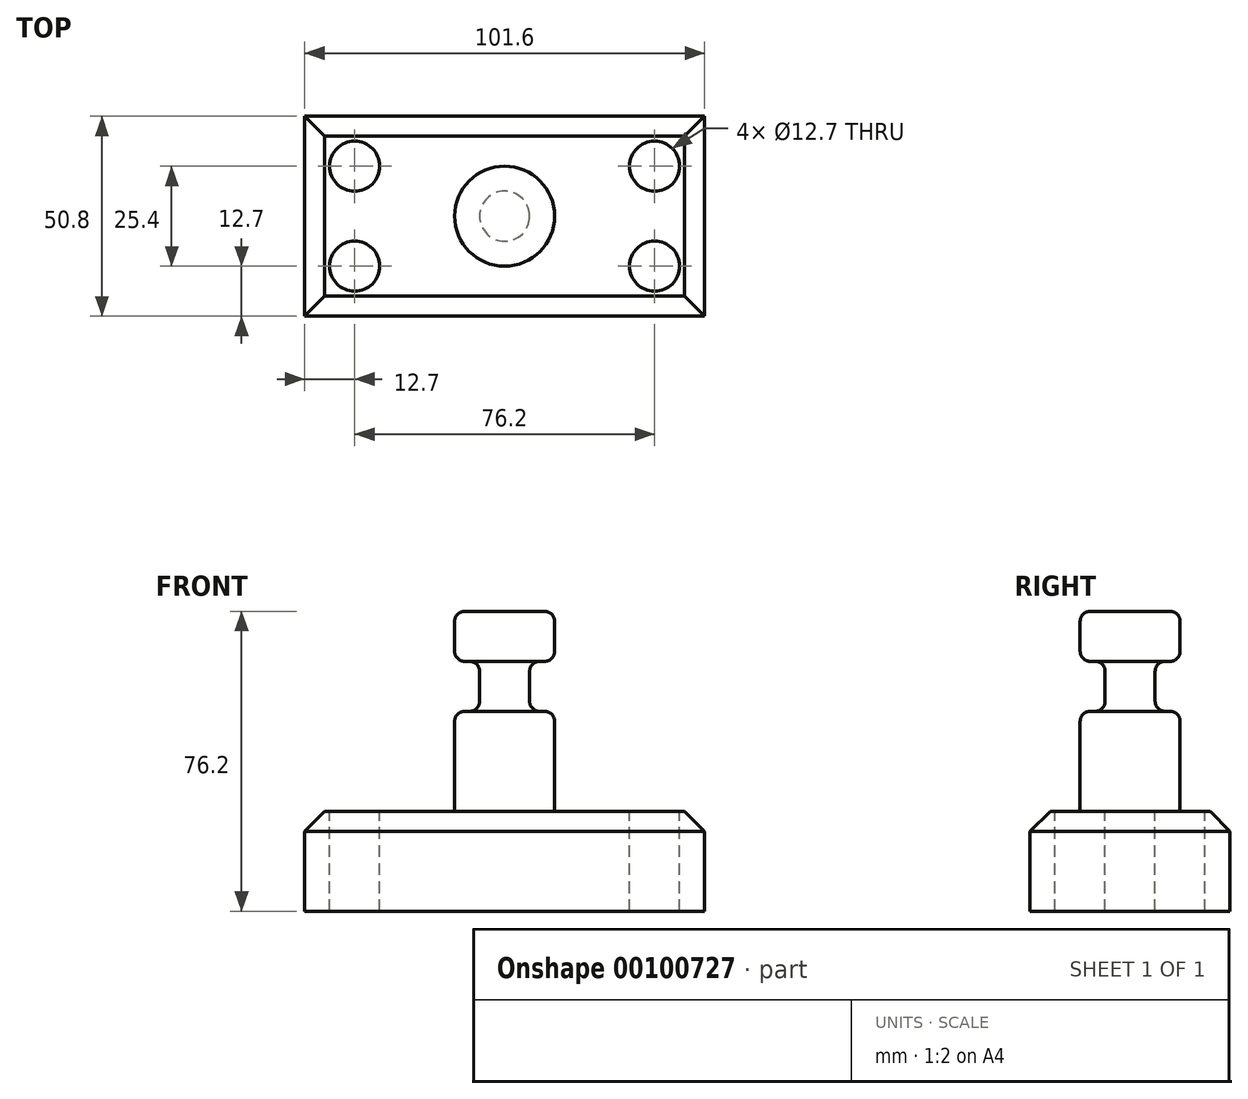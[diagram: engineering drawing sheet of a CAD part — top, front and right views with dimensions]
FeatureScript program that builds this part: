
annotation { "Feature Type Name" : "Feature", "Feature Type Description" : "" }
export const myFeature = defineFeature(function(context is Context, id is Id, definition is map)
    precondition{}
    {
        {
            var Q0;
            Q0=qCreatedBy(makeId("Top.planeOp"),FACE);
            var sketch = newSketch(context, id + "F0", { "sketchPlane" : qUnion([Q0])});
            skLineSegment(sketch, "E0.bottom", {"start": v(-50.8, 25.4) * mm, "end": v(50.8, 25.4) * mm});
            skLineSegment(sketch, "E0.top", {"start": v(-50.8, -25.4) * mm, "end": v(50.8, -25.4) * mm});
            skLineSegment(sketch, "E0.left", {"start": v(-50.8, 25.4) * mm, "end": v(-50.8, -25.4) * mm});
            skLineSegment(sketch, "E0.right", {"start": v(50.8, 25.4) * mm, "end": v(50.8, -25.4) * mm});
            skPoint(sketch, "E0.middle", {"position": v(0, 0) * mm});
            skSolve(sketch);
        }
        {
            var Q0;
            Q0=makeQuery(id+"F0.imprint","IMPRINT",FACE,{"disambiguationData":[TD([[makeQuery(id+"F0.imprint","IMPRINT",EDGE,{"derivedFrom":sQuery(id+"F0.wireOp",EDGE,"E0.bottom")}),-1.0]])]});
            extrude(context, id + "F1", {"entities" : qUnion([Q0]), "depth" : 25.4 * mm});
        }
        {
            var Q0;
            Q0=makeQuery(id+"F1.opExtrude","CAP_FACE",FACE,{"disambiguationData":[OSD([sQuery(id+"F0.wireOp",EDGE,"E0.bottom"),sQuery(id+"F0.wireOp",EDGE,"E0.top"),sQuery(id+"F0.wireOp",EDGE,"E0.left"),sQuery(id+"F0.wireOp",EDGE,"E0.right")])],"isStart":false});
            var sketch = newSketch(context, id + "F2", { "sketchPlane" : qUnion([Q0])});
            skCircle(sketch, "E1", {"center": v(-38.1, 12.7) * mm, "radius": 6.35 * mm});
            skCircle(sketch, "E2", {"center": v(38.1, 12.7) * mm, "radius": 6.35 * mm});
            skCircle(sketch, "E3", {"center": v(38.1, -12.7) * mm, "radius": 6.35 * mm});
            skCircle(sketch, "E4", {"center": v(-38.1, -12.7) * mm, "radius": 6.35 * mm});
            skSolve(sketch);
        }
        {
            var Q0;
            Q0 = qSketchRegion(id + "F2", true);
            extrude(context, id + "F3", {"entities" : qUnion([Q0]), "operationType" : NewBodyOperationType.REMOVE, "endBound" : BoundingType.THROUGH_ALL, "oppositeDirection" : true, "depth" : 25.4 * mm});
        }
        {
            var Q0;
            Q0=qCreatedBy(makeId("Front.planeOp"),FACE);
            var sketch = newSketch(context, id + "F4", { "sketchPlane" : qUnion([Q0])});
            skPoint(sketch, "E5.firstSnap0", {"position": v(0, 25.4) * mm});
            skLineSegment(sketch, "E5.bottom", {"start": v(0, 25.4) * mm, "end": v(-12.7, 25.4) * mm});
            skLineSegment(sketch, "E5.top", {"start": v(0, 76.2) * mm, "end": v(-12.7, 76.2) * mm});
            skLineSegment(sketch, "E5.left", {"start": v(0, 25.4) * mm, "end": v(0, 76.2) * mm});
            skLineSegment(sketch, "E5.right", {"start": v(-12.7, 25.4) * mm, "end": v(-12.7, 76.2) * mm});
            skSolve(sketch);
        }
        {
            var Q0;
            Q0=makeQuery(id+"F4.imprint","IMPRINT",FACE,{"disambiguationData":[TD([[makeQuery(id+"F4.imprint","IMPRINT",EDGE,{"derivedFrom":sQuery(id+"F4.wireOp",EDGE,"E5.bottom")}),1.0]])]});
            var Q1;
            Q1=makeQuery(id+"F4.imprint","IMPRINT",FACE,{"disambiguationData":[TD([[makeQuery(id+"F4.imprint","IMPRINT",EDGE,{"derivedFrom":sQuery(id+"F4.wireOp",EDGE,"E5.bottom")}),-1.0]])]});
            var Q2;
            Q2=sQuery(id+"F4.wireOp",EDGE,"E5.left");
            revolve(context, id + "F5", {"operationType" : NewBodyOperationType.ADD, "entities" : qUnion([Q0, Q1]), "axis" : qUnion([Q2]), "revolveType" : RevolveType.FULL});
        }
        {
            var Q0;
            Q0=qCreatedBy(makeId("Front.planeOp"),FACE);
            var sketch = newSketch(context, id + "F6", { "sketchPlane" : qUnion([Q0])});
            skLineSegment(sketch, "E6.bottom", {"start": v(-19.05, 63.5) * mm, "end": v(-6.35, 63.5) * mm});
            skLineSegment(sketch, "E6.top", {"start": v(-19.05, 50.8) * mm, "end": v(-6.35, 50.8) * mm});
            skLineSegment(sketch, "E6.left", {"start": v(-19.05, 63.5) * mm, "end": v(-19.05, 50.8) * mm});
            skLineSegment(sketch, "E6.right", {"start": v(-6.35, 63.5) * mm, "end": v(-6.35, 50.8) * mm});
            skLineSegment(sketch, "E7", {"start": v(0, 0) * mm, "end": v(0, 88.96) * mm, "construction": true});
            skSolve(sketch);
        }
        {
            var Q0;
            Q0 = qSketchRegion(id + "F6", true);
            var Q1;
            Q1=sQuery(id+"F6.wireOp",EDGE,"E7");
            revolve(context, id + "F7", {"operationType" : NewBodyOperationType.REMOVE, "entities" : qUnion([Q0]), "axis" : qUnion([Q1]), "revolveType" : RevolveType.FULL, "oppositeDirection" : true});
        }
        {
            var Q0;
            Q0=makeQuery(id+"F7.boolean.opBoolean","INTERSECT",EDGE,{"derivedFrom":[makeQuery(id+"F5.opRevolve","SWEPT_FACE",FACE,{"disambiguationData":[OSD([sQuery(id+"F4.wireOp",EDGE,"E5.right")])]}),makeQuery(id+"F7.opRevolve","SWEPT_FACE",FACE,{"disambiguationData":[OSD([sQuery(id+"F6.wireOp",EDGE,"E6.top")])]})]});
            var Q1;
            Q1=makeQuery(id+"F7.boolean.opBoolean","COPY",EDGE,{"derivedFrom":makeQuery(id+"F7.opRevolve","SWEPT_EDGE",EDGE,{"disambiguationData":[OSD([sQuery(id+"F6.wireOp",EDGE,"E6.top"),sQuery(id+"F6.wireOp",EDGE,"E6.right")])]})});
            var Q2;
            Q2=makeQuery(id+"F7.boolean.opBoolean","INTERSECT",EDGE,{"derivedFrom":[makeQuery(id+"F5.opRevolve","SWEPT_FACE",FACE,{"disambiguationData":[OSD([sQuery(id+"F4.wireOp",EDGE,"E5.right")])]}),makeQuery(id+"F7.opRevolve","SWEPT_FACE",FACE,{"disambiguationData":[OSD([sQuery(id+"F6.wireOp",EDGE,"E6.bottom")])]})]});
            var Q3;
            Q3=makeQuery(id+"F7.boolean.opBoolean","COPY",EDGE,{"derivedFrom":makeQuery(id+"F7.opRevolve","SWEPT_EDGE",EDGE,{"disambiguationData":[OSD([sQuery(id+"F6.wireOp",EDGE,"E6.bottom"),sQuery(id+"F6.wireOp",EDGE,"E6.right")])]})});
            var Q4;
            Q4=makeQuery(id+"F5.opRevolve","SWEPT_EDGE",EDGE,{"disambiguationData":[OSD([sQuery(id+"F4.wireOp",EDGE,"E5.bottom"),sQuery(id+"F4.wireOp",EDGE,"E5.right")])]});
            var Q5;
            Q5=makeQuery(id+"F5.opRevolve","SWEPT_EDGE",EDGE,{"disambiguationData":[OSD([sQuery(id+"F4.wireOp",EDGE,"E5.top"),sQuery(id+"F4.wireOp",EDGE,"E5.right")])]});
            fillet(context, id + "F8", {"entities" : qUnion([Q0, Q1, Q2, Q3, Q4, Q5]), "radius" : 2.54 * mm, "tangentPropagation" : true, "allowEdgeOverflow" : false});
        }
        {
            var Q0;
            Q0=makeQuery(id+"F1.opExtrude","CAP_EDGE",EDGE,{"disambiguationData":[OSD([sQuery(id+"F0.wireOp",EDGE,"E0.bottom")])],"isStart":false});
            var Q1;
            Q1=makeQuery(id+"F1.opExtrude","CAP_EDGE",EDGE,{"disambiguationData":[OSD([sQuery(id+"F0.wireOp",EDGE,"E0.right")])],"isStart":false});
            var Q2;
            Q2=makeQuery(id+"F1.opExtrude","CAP_EDGE",EDGE,{"disambiguationData":[OSD([sQuery(id+"F0.wireOp",EDGE,"E0.top")])],"isStart":false});
            var Q3;
            Q3=makeQuery(id+"F1.opExtrude","CAP_EDGE",EDGE,{"disambiguationData":[OSD([sQuery(id+"F0.wireOp",EDGE,"E0.left")])],"isStart":false});
            chamfer(context, id + "F9", {"entities" : qUnion([Q0, Q1, Q2, Q3]), "width" : 5.08 * mm, "tangentPropagation" : true});
        }
    });
